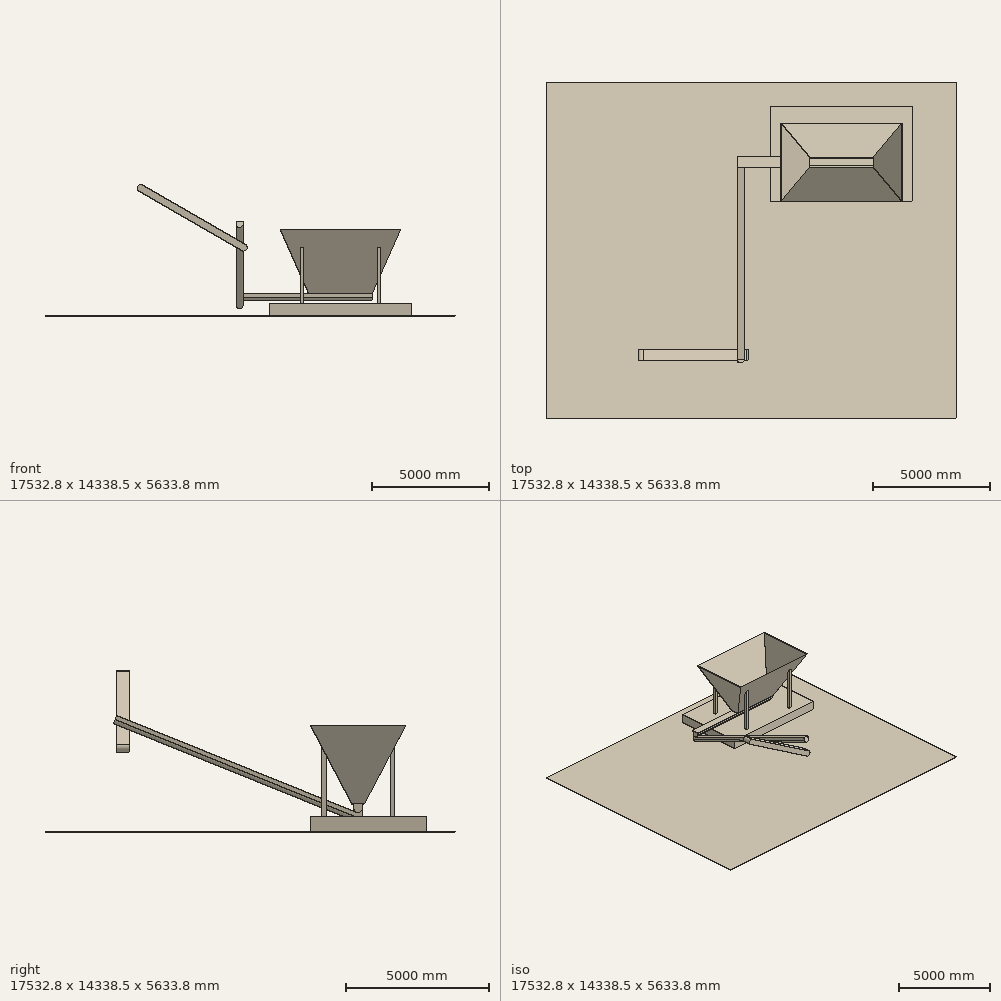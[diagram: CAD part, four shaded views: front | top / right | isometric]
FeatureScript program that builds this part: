
annotation { "Feature Type Name" : "Feature", "Feature Type Description" : "" }
export const myFeature = defineFeature(function(context is Context, id is Id, definition is map)
    precondition{}
    {
        {
            var Q0;
            Q0=qCreatedBy(makeId("Top.planeOp"),FACE);
            var sketch = newSketch(context, id + "F0", { "sketchPlane" : qUnion([Q0])});
            skLineSegment(sketch, "E0.bottom", {"start": v(-12618.18, 5075.63) * mm, "end": v(4914.6, 5075.63) * mm});
            skLineSegment(sketch, "E0.top", {"start": v(-12618.18, -9262.92) * mm, "end": v(4914.6, -9262.92) * mm});
            skLineSegment(sketch, "E0.left", {"start": v(-12618.18, 5075.63) * mm, "end": v(-12618.18, -9262.92) * mm});
            skLineSegment(sketch, "E0.right", {"start": v(4914.6, 5075.63) * mm, "end": v(4914.6, -9262.92) * mm});
            skSolve(sketch);
        }
        {
            var Q0;
            Q0=makeQuery(id+"F0.imprint","IMPRINT",FACE,{"disambiguationData":[TD([[makeQuery(id+"F0.imprint","IMPRINT",EDGE,{"derivedFrom":sQuery(id+"F0.wireOp",EDGE,"E0.bottom")}),-1.0]])]});
            extrude(context, id + "F1", {"entities" : qUnion([Q0]), "oppositeDirection" : true, "depth" : 25.4 * mm});
        }
        {
            var Q0;
            Q0=qCreatedBy(makeId("Front.planeOp"),FACE);
            var sketch = newSketch(context, id + "F2", { "sketchPlane" : qUnion([Q0])});
            skLineSegment(sketch, "E1.bottom", {"start": v(-2590.8, 3708.4) * mm, "end": v(2590.8, 3708.4) * mm});
            skLineSegment(sketch, "E1.top", {"start": v(-1371.6, 965.2) * mm, "end": v(1371.6, 965.2) * mm});
            skLineSegment(sketch, "E2", {"start": v(-2590.8, 3708.4) * mm, "end": v(-1371.6, 965.2) * mm});
            skLineSegment(sketch, "E3", {"start": v(2590.8, 3708.4) * mm, "end": v(1371.6, 965.2) * mm});
            skSolve(sketch);
        }
        {
            var Q0;
            Q0=makeQuery(id+"F2.imprint","IMPRINT",FACE,{"disambiguationData":[TD([[makeQuery(id+"F2.imprint","IMPRINT",EDGE,{"derivedFrom":sQuery(id+"F2.wireOp",EDGE,"E1.bottom")}),-1.0]])]});
            extrude(context, id + "F3", {"entities" : qUnion([Q0]), "oppositeDirection" : true, "depth" : 3352.8 * mm});
        }
        {
            var Q0;
            Q0=qCreatedBy(makeId("Right.planeOp"),FACE);
            var sketch = newSketch(context, id + "F4", { "sketchPlane" : qUnion([Q0])});
            skLineSegment(sketch, "E4.0.1", {"start": v(1447.8, 965.2) * mm, "end": v(1905, 965.2) * mm});
            skLineSegment(sketch, "E4.0.3", {"start": v(3352.8, 3708.4) * mm, "end": v(0, 3708.4) * mm});
            skLineSegment(sketch, "E5", {"start": v(0, 3708.4) * mm, "end": v(1447.8, 965.2) * mm});
            skLineSegment(sketch, "E6", {"start": v(3352.8, 3708.4) * mm, "end": v(1905, 965.2) * mm});
            skLineSegment(sketch, "E7", {"start": v(0, 3708.4) * mm, "end": v(0, 965.2) * mm});
            skLineSegment(sketch, "E8", {"start": v(0, 965.2) * mm, "end": v(1447.8, 965.2) * mm});
            skLineSegment(sketch, "E9", {"start": v(3352.8, 3708.4) * mm, "end": v(3352.8, 965.2) * mm});
            skLineSegment(sketch, "E10", {"start": v(1905, 965.2) * mm, "end": v(3352.8, 965.2) * mm});
            skSolve(sketch);
        }
        {
            var Q0;
            Q0=makeQuery(id+"F4.imprint","IMPRINT",FACE,{"disambiguationData":[TD([[makeQuery(id+"F4.imprint","IMPRINT",EDGE,{"derivedFrom":sQuery(id+"F4.wireOp",EDGE,"E5")}),-1.0]])]});
            var Q1;
            Q1=makeQuery(id+"F4.imprint","IMPRINT",FACE,{"disambiguationData":[TD([[makeQuery(id+"F4.imprint","IMPRINT",EDGE,{"derivedFrom":sQuery(id+"F4.wireOp",EDGE,"E6")}),1.0]])]});
            extrude(context, id + "F5", {"entities" : qUnion([Q0, Q1]), "operationType" : NewBodyOperationType.REMOVE, "endBound" : BoundingType.SYMMETRIC, "depth" : 7620 * mm});
        }
        {
            var Q0;
            Q0=makeQuery(id+"F3.opExtrude","SWEPT_FACE",FACE,{"disambiguationData":[OSD([sQuery(id+"F2.wireOp",EDGE,"E1.bottom")])]});
            shell(context, id + "F6", {"entities" : qUnion([Q0]), "thickness" : 12.7 * mm});
        }
        {
            var Q0;
            Q0=makeQuery(id+"F3.opExtrude","SWEPT_FACE",FACE,{"disambiguationData":[OSD([sQuery(id+"F2.wireOp",EDGE,"E1.top")])]});
            var sketch = newSketch(context, id + "F7", { "sketchPlane" : qUnion([Q0])});
            skLineSegment(sketch, "E11.0.0", {"start": v(-1371.6, -1905) * mm, "end": v(1371.6, -1905) * mm});
            skLineSegment(sketch, "E11.0.1", {"start": v(1371.6, -1905) * mm, "end": v(1371.6, -1447.8) * mm});
            skLineSegment(sketch, "E11.0.2", {"start": v(1371.6, -1447.8) * mm, "end": v(-1371.6, -1447.8) * mm});
            skLineSegment(sketch, "E11.0.3", {"start": v(-1371.6, -1447.8) * mm, "end": v(-1371.6, -1905) * mm});
            skLineSegment(sketch, "E12.0", {"start": v(-1358.9, -1892.3) * mm, "end": v(1358.9, -1892.3) * mm});
            skLineSegment(sketch, "E12.1", {"start": v(-1358.9, -1460.5) * mm, "end": v(-1358.9, -1892.3) * mm});
            skLineSegment(sketch, "E12.2", {"start": v(1358.9, -1460.5) * mm, "end": v(-1358.9, -1460.5) * mm});
            skLineSegment(sketch, "E12.3", {"start": v(1358.9, -1892.3) * mm, "end": v(1358.9, -1460.5) * mm});
            skSolve(sketch);
        }
        {
            var Q0;
            Q0=makeQuery(id+"F7.imprint","IMPRINT",FACE,{"disambiguationData":[TD([[makeQuery(id+"F7.imprint","IMPRINT",EDGE,{"derivedFrom":sQuery(id+"F7.wireOp",EDGE,"E12.0")}),1.0]])]});
            extrude(context, id + "F8", {"entities" : qUnion([Q0]), "operationType" : NewBodyOperationType.REMOVE, "endBound" : BoundingType.THROUGH_ALL, "oppositeDirection" : true, "depth" : 25.4 * mm});
        }
        {
            var Q0;
            Q0=qCreatedBy(makeId("Top.planeOp"),FACE);
            var sketch = newSketch(context, id + "F9", { "sketchPlane" : qUnion([Q0])});
            skLineSegment(sketch, "E13.bottom", {"start": v(-1727.2, 406.4) * mm, "end": v(1727.2, 406.4) * mm, "construction": true});
            skLineSegment(sketch, "E13.top", {"start": v(-1727.2, 2946.4) * mm, "end": v(1727.2, 2946.4) * mm, "construction": true});
            skLineSegment(sketch, "E13.left", {"start": v(-1727.2, 406.4) * mm, "end": v(-1727.2, 2946.4) * mm, "construction": true});
            skLineSegment(sketch, "E13.right", {"start": v(1727.2, 406.4) * mm, "end": v(1727.2, 2946.4) * mm, "construction": true});
            skLineSegment(sketch, "E14.bottom", {"start": v(-1727.2, 406.4) * mm, "end": v(-1574.8, 406.4) * mm});
            skLineSegment(sketch, "E14.top", {"start": v(-1727.2, 558.8) * mm, "end": v(-1574.8, 558.8) * mm});
            skLineSegment(sketch, "E14.left", {"start": v(-1727.2, 406.4) * mm, "end": v(-1727.2, 558.8) * mm});
            skLineSegment(sketch, "E14.right", {"start": v(-1574.8, 406.4) * mm, "end": v(-1574.8, 558.8) * mm});
            skLineSegment(sketch, "E15.bottom", {"start": v(1727.2, 406.4) * mm, "end": v(1574.8, 406.4) * mm});
            skLineSegment(sketch, "E15.top", {"start": v(1727.2, 558.8) * mm, "end": v(1574.8, 558.8) * mm});
            skLineSegment(sketch, "E15.left", {"start": v(1727.2, 406.4) * mm, "end": v(1727.2, 558.8) * mm});
            skLineSegment(sketch, "E15.right", {"start": v(1574.8, 406.4) * mm, "end": v(1574.8, 558.8) * mm});
            skLineSegment(sketch, "E16.bottom", {"start": v(1727.2, 2946.4) * mm, "end": v(1574.8, 2946.4) * mm});
            skLineSegment(sketch, "E16.top", {"start": v(1727.2, 2794) * mm, "end": v(1574.8, 2794) * mm});
            skLineSegment(sketch, "E16.left", {"start": v(1727.2, 2946.4) * mm, "end": v(1727.2, 2794) * mm});
            skLineSegment(sketch, "E16.right", {"start": v(1574.8, 2946.4) * mm, "end": v(1574.8, 2794) * mm});
            skLineSegment(sketch, "E17.bottom", {"start": v(-1727.2, 2946.4) * mm, "end": v(-1574.8, 2946.4) * mm});
            skLineSegment(sketch, "E17.top", {"start": v(-1727.2, 2794) * mm, "end": v(-1574.8, 2794) * mm});
            skLineSegment(sketch, "E17.left", {"start": v(-1727.2, 2946.4) * mm, "end": v(-1727.2, 2794) * mm});
            skLineSegment(sketch, "E17.right", {"start": v(-1574.8, 2946.4) * mm, "end": v(-1574.8, 2794) * mm});
            skSolve(sketch);
        }
        {
            var Q0;
            Q0=makeQuery(id+"F9.imprint","IMPRINT",FACE,{"disambiguationData":[TD([[makeQuery(id+"F9.imprint","IMPRINT",EDGE,{"derivedFrom":sQuery(id+"F9.wireOp",EDGE,"E14.bottom")}),1.0]])]});
            var Q1;
            Q1=makeQuery(id+"F9.imprint","IMPRINT",FACE,{"disambiguationData":[TD([[makeQuery(id+"F9.imprint","IMPRINT",EDGE,{"derivedFrom":sQuery(id+"F9.wireOp",EDGE,"E15.bottom")}),-1.0]])]});
            var Q2;
            Q2=makeQuery(id+"F9.imprint","IMPRINT",FACE,{"disambiguationData":[TD([[makeQuery(id+"F9.imprint","IMPRINT",EDGE,{"derivedFrom":sQuery(id+"F9.wireOp",EDGE,"E16.bottom")}),1.0]])]});
            var Q3;
            Q3=makeQuery(id+"F9.imprint","IMPRINT",FACE,{"disambiguationData":[TD([[makeQuery(id+"F9.imprint","IMPRINT",EDGE,{"derivedFrom":sQuery(id+"F9.wireOp",EDGE,"E17.bottom")}),-1.0]])]});
            extrude(context, id + "F10", {"entities" : qUnion([Q0, Q1, Q2, Q3]), "operationType" : NewBodyOperationType.ADD, "endBound" : BoundingType.UP_TO_NEXT, "depth" : 25.4 * mm});
        }
        {
            var Q0;
            Q0=qCreatedBy(makeId("Front.planeOp"),FACE);
            cPlane(context, id + "F11", {"entities" : qUnion([Q0]), "cplaneType" : CPlaneType.OFFSET, "offset" : 6553.2 * mm, "width" : 152.4 * mm, "height" : 152.4 * mm});
        }
        {
            var Q0;
            Q0=qCreatedBy(id+"F11.planeOp",FACE);
            var sketch = newSketch(context, id + "F12", { "sketchPlane" : qUnion([Q0])});
            skLineSegment(sketch, "E18", {"start": v(0, 0) * mm, "end": v(-4064, 0) * mm, "construction": true});
            skLineSegment(sketch, "E19", {"start": v(-4064, 0) * mm, "end": v(-4064, 3048) * mm, "construction": true});
            skLineSegment(sketch, "E20", {"start": v(-4064, 3048) * mm, "end": v(-8463.4, 5588) * mm});
            skLineSegment(sketch, "E21", {"start": v(-8615.8, 5324.04) * mm, "end": v(-4216.4, 2784.04) * mm});
            skArc(sketch, "E22", {"start": v(-8463.4, 5588) * mm, "mid": v(-8671.6, 5532.22) * mm, "end": v(-8615.8, 5324.04) * mm});
            skArc(sketch, "E23", {"start": v(-4216.4, 2784.04) * mm, "mid": v(-4008.22, 2839.82) * mm, "end": v(-4064, 3048) * mm});
            skSolve(sketch);
        }
        {
            var Q0;
            Q0=makeQuery(id+"F12.imprint","IMPRINT",FACE,{"disambiguationData":[TD([[makeQuery(id+"F12.imprint","IMPRINT",EDGE,{"derivedFrom":sQuery(id+"F12.wireOp",EDGE,"E20")}),1.0]])]});
            extrude(context, id + "F13", {"entities" : qUnion([Q0]), "endBound" : BoundingType.SYMMETRIC, "depth" : 457.2 * mm});
        }
        {
            var Q0;
            Q0=makeQuery(id+"F3.opExtrude","SWEPT_FACE",FACE,{"disambiguationData":[OSD([sQuery(id+"F2.wireOp",EDGE,"E1.top")])]});
            var sketch = newSketch(context, id + "F14", { "sketchPlane" : qUnion([Q0])});
            skLineSegment(sketch, "E24.0.0", {"start": v(-1371.6, -1905) * mm, "end": v(1371.6, -1905) * mm});
            skLineSegment(sketch, "E24.0.1", {"start": v(1371.6, -1905) * mm, "end": v(1371.6, -1447.8) * mm});
            skLineSegment(sketch, "E24.0.2", {"start": v(1371.6, -1447.8) * mm, "end": v(-1371.6, -1447.8) * mm});
            skLineSegment(sketch, "E25", {"start": v(-1371.6, -1447.8) * mm, "end": v(-4465.42, -1447.8) * mm});
            skLineSegment(sketch, "E26", {"start": v(-4465.42, -1447.8) * mm, "end": v(-4465.42, -1905) * mm});
            skLineSegment(sketch, "E27", {"start": v(-1371.6, -1905) * mm, "end": v(-4465.42, -1905) * mm});
            skSolve(sketch);
        }
        {
            var Q0;
            Q0=makeQuery(id+"F14.imprint","IMPRINT",FACE,{"disambiguationData":[TD([[makeQuery(id+"F14.imprint","IMPRINT",EDGE,{"derivedFrom":makeQuery(id+"F8.boolean.opBoolean","COPY",EDGE,{"derivedFrom":makeQuery(id+"F8.opExtrude","CAP_EDGE",EDGE,{"disambiguationData":[OSD([sQuery(id+"F7.wireOp",EDGE,"E12.0")])],"isStart":true})})}),1.0]])]});
            var Q1;
            Q1=makeQuery(id+"F14.imprint","IMPRINT",FACE,{"disambiguationData":[TD([[makeQuery(id+"F14.imprint","IMPRINT",EDGE,{"derivedFrom":sQuery(id+"F14.wireOp",EDGE,"E25")}),1.0]])]});
            var Q2;
            Q2=makeQuery(id+"F14.imprint","IMPRINT",FACE,{"disambiguationData":[TD([[makeQuery(id+"F14.imprint","IMPRINT",EDGE,{"derivedFrom":sQuery(id+"F14.wireOp",EDGE,"E24.0.0")}),-1.0]])]});
            extrude(context, id + "F15", {"entities" : qUnion([Q0, Q1, Q2]), "depth" : 12.7 * mm});
        }
        {
            var Q0;
            Q0=makeQuery(id+"F15.opExtrude","CAP_FACE",FACE,{"disambiguationData":[OSD([sQuery(id+"F14.wireOp",EDGE,"E24.0.0"),sQuery(id+"F14.wireOp",EDGE,"E24.0.1"),sQuery(id+"F14.wireOp",EDGE,"E24.0.2"),sQuery(id+"F14.wireOp",EDGE,"E25"),sQuery(id+"F14.wireOp",EDGE,"E26"),sQuery(id+"F14.wireOp",EDGE,"E27")])],"isStart":false});
            var sketch = newSketch(context, id + "F16", { "sketchPlane" : qUnion([Q0])});
            skLineSegment(sketch, "E28", {"start": v(-4465.42, -1524) * mm, "end": v(1371.6, -1524) * mm});
            skLineSegment(sketch, "E29", {"start": v(-4465.42, -1828.8) * mm, "end": v(1371.6, -1828.8) * mm});
            skSolve(sketch);
        }
        {
            var Q0;
            {var subQ0=sQuery(id+"F16.wireOp",EDGE,"E28");Q0=makeQuery(id+"F16.imprint","IMPRINT",FACE,{"disambiguationData":[TD([[makeQuery(id+"F16.imprint","IMPRINT",EDGE,{"derivedFrom":subQ0}),-1.0]])]});}
            extrude(context, id + "F17", {"entities" : qUnion([Q0]), "operationType" : NewBodyOperationType.ADD, "depth" : 304.8 * mm});
        }
        {
            var Q0;
            Q0=makeQuery(id+"F17.opExtrude","CAP_EDGE",EDGE,{"disambiguationData":[OSD([sQuery(id+"F16.wireOp",EDGE,"E28")])],"isStart":false});
            var Q1;
            Q1=makeQuery(id+"F17.opExtrude","CAP_EDGE",EDGE,{"disambiguationData":[OSD([sQuery(id+"F16.wireOp",EDGE,"E29")])],"isStart":false});
            fillet(context, id + "F18", {"entities" : qUnion([Q0, Q1]), "radius" : 152.4 * mm, "tangentPropagation" : true, "allowEdgeOverflow" : false});
        }
        {
            var Q0;
            Q0=makeQuery(id+"F15.opExtrude","SWEPT_FACE",FACE,{"disambiguationData":[OSD([sQuery(id+"F14.wireOp",EDGE,"E26")])]});
            var sketch = newSketch(context, id + "F19", { "sketchPlane" : qUnion([Q0])});
            skLineSegment(sketch, "E30", {"start": v(-1828.8, 574.16) * mm, "end": v(6767.12, 4047.14) * mm});
            skLineSegment(sketch, "E31", {"start": v(6767.12, 4047.14) * mm, "end": v(6881.3, 3764.53) * mm});
            skLineSegment(sketch, "E32", {"start": v(6881.3, 3764.53) * mm, "end": v(-1714.62, 291.55) * mm});
            skLineSegment(sketch, "E33", {"start": v(-1828.8, 574.16) * mm, "end": v(-1714.62, 291.55) * mm});
            skLineSegment(sketch, "E34", {"start": v(-1714.62, 291.55) * mm, "end": v(4664.1, 291.55) * mm, "construction": true});
            skLineSegment(sketch, "E35", {"start": v(-1828.8, 574.16) * mm, "end": v(-1828.8, 800.1) * mm});
            skSolve(sketch);
        }
        {
            var Q0;
            {var subQ0=sQuery(id+"F19.wireOp",EDGE,"E31");Q0=makeQuery(id+"F19.imprint","IMPRINT",FACE,{"disambiguationData":[TD([[makeQuery(id+"F19.imprint","IMPRINT",EDGE,{"derivedFrom":subQ0}),-1.0]])]});}
            var Q1;
            {var subQ0=sQuery(id+"F19.wireOp",EDGE,"E35");Q1=makeQuery(id+"F19.imprint","IMPRINT",FACE,{"disambiguationData":[TD([[makeQuery(id+"F19.imprint","IMPRINT",EDGE,{"derivedFrom":subQ0}),-1.0]])]});}
            extrude(context, id + "F20", {"entities" : qUnion([Q0, Q1]), "oppositeDirection" : true, "depth" : 304.8 * mm});
        }
        {
            var Q0;
            Q0=makeQuery(id+"F20.opExtrude","CAP_EDGE",EDGE,{"disambiguationData":[OSD([sQuery(id+"F19.wireOp",EDGE,"E32")])],"isStart":true});
            var Q1;
            Q1=makeQuery(id+"F20.opExtrude","CAP_EDGE",EDGE,{"disambiguationData":[OSD([sQuery(id+"F19.wireOp",EDGE,"E32")])],"isStart":false});
            fillet(context, id + "F21", {"entities" : qUnion([Q0, Q1]), "radius" : 152.4 * mm, "tangentPropagation" : true, "allowEdgeOverflow" : false});
        }
        {
            var Q0;
            Q0=makeQuery(id+"F1.opExtrude","CAP_FACE",FACE,{"disambiguationData":[OSD([sQuery(id+"F0.wireOp",EDGE,"E0.bottom"),sQuery(id+"F0.wireOp",EDGE,"E0.top"),sQuery(id+"F0.wireOp",EDGE,"E0.left"),sQuery(id+"F0.wireOp",EDGE,"E0.right")])],"isStart":true});
            var sketch = newSketch(context, id + "F22", { "sketchPlane" : qUnion([Q0])});
            skLineSegment(sketch, "E36.bottom", {"start": v(-3048, 4064) * mm, "end": v(3048, 4064) * mm});
            skLineSegment(sketch, "E36.top", {"start": v(-3048, 0) * mm, "end": v(3048, 0) * mm});
            skLineSegment(sketch, "E36.left", {"start": v(-3048, 4064) * mm, "end": v(-3048, 0) * mm});
            skLineSegment(sketch, "E36.right", {"start": v(3048, 4064) * mm, "end": v(3048, 0) * mm});
            skSolve(sketch);
        }
        {
            var Q0;
            Q0=makeQuery(id+"F22.imprint","IMPRINT",FACE,{"disambiguationData":[TD([[makeQuery(id+"F22.imprint","IMPRINT",EDGE,{"derivedFrom":sQuery(id+"F22.wireOp",EDGE,"E36.bottom")}),-1.0]])]});
            extrude(context, id + "F23", {"entities" : qUnion([Q0]), "depth" : 508 * mm});
        }
    });
